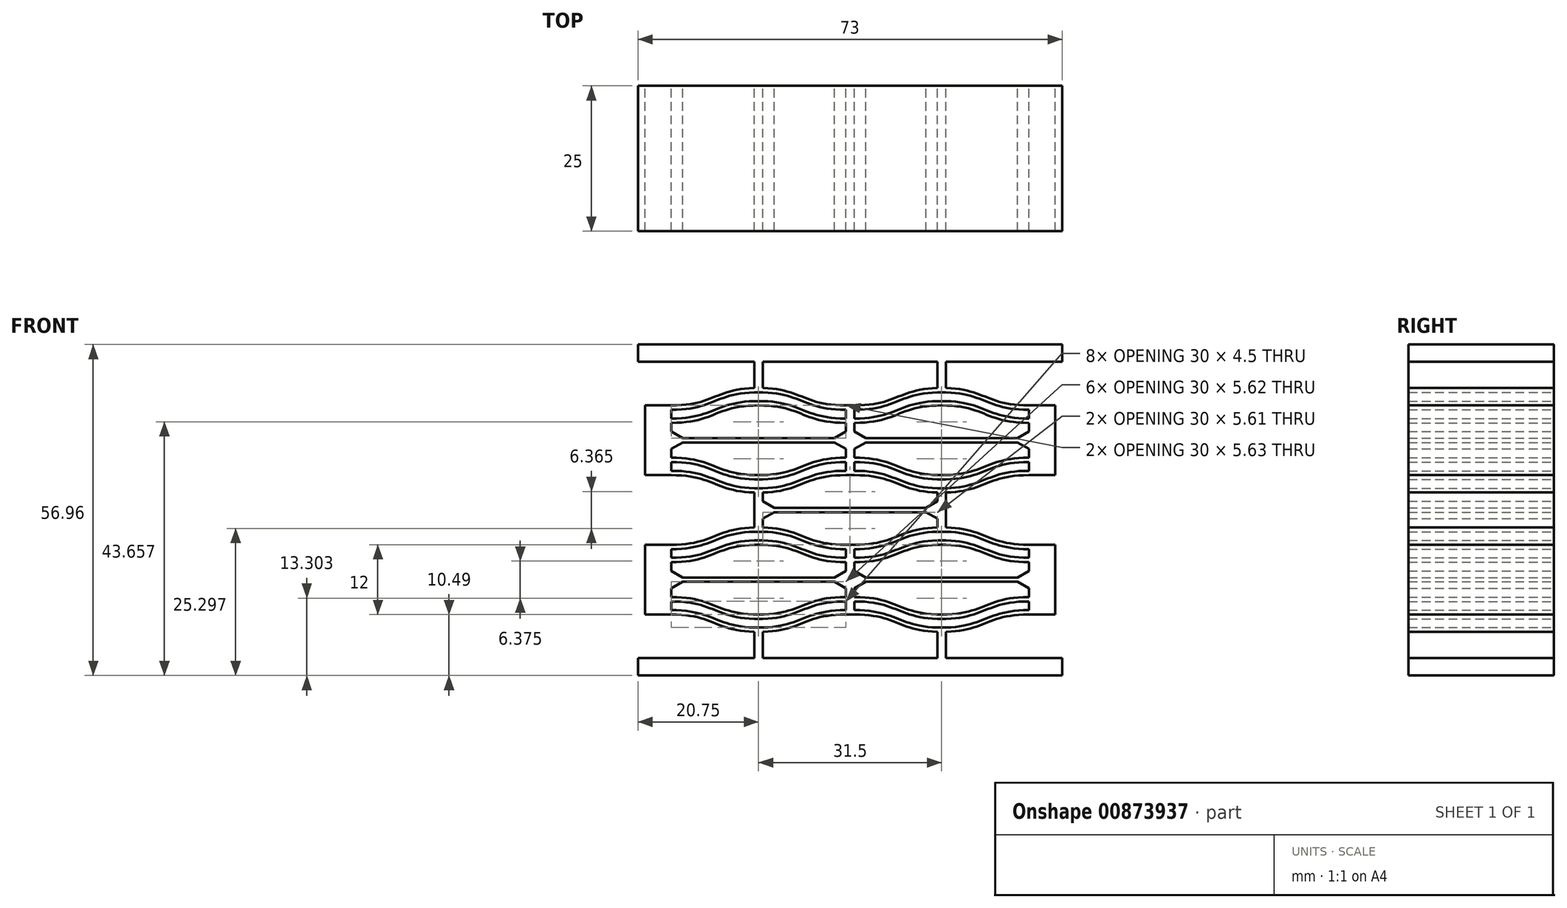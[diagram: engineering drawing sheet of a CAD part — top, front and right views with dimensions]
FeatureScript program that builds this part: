
annotation { "Feature Type Name" : "Feature", "Feature Type Description" : "" }
export const myFeature = defineFeature(function(context is Context, id is Id, definition is map)
    precondition{}
    {
        {
            var Q0;
            Q0=qCreatedBy(makeId("Front.planeOp"),FACE);
            var sketch = newSketch(context, id + "F0", { "sketchPlane" : qUnion([Q0])});
            skLineSegment(sketch, "E0", {"start": v(0, 11.25) * mm, "end": v(0, 9.75) * mm});
            skLineSegment(sketch, "E1", {"start": v(0, 0) * mm, "end": v(1.5, 0) * mm});
            skLineSegment(sketch, "E2", {"start": v(33, 12) * mm, "end": v(31.5, 12) * mm});
            skLineSegment(sketch, "E3", {"start": v(33, 0) * mm, "end": v(31.5, 0) * mm});
            skPoint(sketch, "E4", {"position": v(0, 6) * mm});
            skLineSegment(sketch, "E5", {"start": v(1.5, 11.25) * mm, "end": v(1.5, 9.75) * mm});
            skLineSegment(sketch, "E6", {"start": v(31.5, 11.25) * mm, "end": v(31.5, 9.75) * mm});
            skPoint(sketch, "E7", {"position": v(0, 7.5) * mm});
            skPoint(sketch, "E8", {"position": v(0, 4.5) * mm});
            skLineSegment(sketch, "E9", {"start": v(1.5, 4.5) * mm, "end": v(3.45, 5.62) * mm});
            skLineSegment(sketch, "E10", {"start": v(1.5, 7.5) * mm, "end": v(3.45, 6.38) * mm});
            skPoint(sketch, "E11", {"position": v(31.5, 4.5) * mm});
            skPoint(sketch, "E12", {"position": v(31.5, 7.5) * mm});
            skLineSegment(sketch, "E13", {"start": v(31.5, 7.5) * mm, "end": v(29.55, 6.38) * mm});
            skLineSegment(sketch, "E14", {"start": v(29.55, 5.63) * mm, "end": v(31.5, 4.5) * mm});
            skPoint(sketch, "E15.positionSnap0", {"position": v(16.5, 6.38) * mm});
            skPoint(sketch, "E16", {"position": v(0, 9) * mm});
            skPoint(sketch, "E17", {"position": v(0, 3) * mm});
            skPoint(sketch, "E18", {"position": v(0, 9.75) * mm});
            skPoint(sketch, "E19", {"position": v(0, 2.25) * mm});
            skPoint(sketch, "E20", {"position": v(1.5, 11.25) * mm});
            skPoint(sketch, "E21", {"position": v(1.5, 0.75) * mm});
            skPoint(sketch, "E22", {"position": v(1.5, 9.75) * mm});
            skPoint(sketch, "E23", {"position": v(1.5, 9) * mm});
            skPoint(sketch, "E24", {"position": v(1.5, 2.25) * mm});
            skPoint(sketch, "E25", {"position": v(1.5, 3) * mm});
            skPoint(sketch, "E26", {"position": v(31.5, 11.25) * mm});
            skPoint(sketch, "E27", {"position": v(31.5, 9.75) * mm});
            skPoint(sketch, "E28", {"position": v(31.5, 9) * mm});
            skPoint(sketch, "E29", {"position": v(31.5, 3) * mm});
            skPoint(sketch, "E30", {"position": v(31.5, 2.25) * mm});
            skPoint(sketch, "E31", {"position": v(31.5, 0.75) * mm});
            skLineSegment(sketch, "E32.trimOffspring", {"start": v(3.45, 6.38) * mm, "end": v(16.5, 6.38) * mm});
            skLineSegment(sketch, "E33.trimOffspring", {"start": v(3.45, 5.62) * mm, "end": v(29.55, 5.63) * mm});
            skPoint(sketch, "E34.start.orphan", {"position": v(0, 5.62) * mm});
            skLineSegment(sketch, "E35.trimOffspring", {"start": v(1.5, 9) * mm, "end": v(1.5, 7.5) * mm});
            skLineSegment(sketch, "E36.trimOffspring", {"start": v(1.5, 2.25) * mm, "end": v(1.5, 0.75) * mm});
            skLineSegment(sketch, "E37.trimOffspring", {"start": v(31.5, 9) * mm, "end": v(31.5, 7.5) * mm});
            skLineSegment(sketch, "E38.trimOffspring", {"start": v(31.5, 2.25) * mm, "end": v(31.5, 0.75) * mm});
            skLineSegment(sketch, "E39.trimOffspring", {"start": v(1.5, 4.5) * mm, "end": v(1.5, 3) * mm});
            skLineSegment(sketch, "E40.trimOffspring", {"start": v(31.5, 4.5) * mm, "end": v(31.5, 3) * mm});
            skLineSegment(sketch, "E41", {"start": v(16.5, 6.38) * mm, "end": v(29.55, 6.38) * mm});
            skPoint(sketch, "E42", {"position": v(16.5, 9) * mm});
            skPoint(sketch, "E43", {"position": v(16.5, 12) * mm});
            skPoint(sketch, "E44", {"position": v(9, 9) * mm});
            skPoint(sketch, "E45", {"position": v(9, 10.5) * mm});
            skPoint(sketch, "E46", {"position": v(24, 10.5) * mm});
            skFitSpline(sketch, "E47", {"points": [v(1.5, 9) * mm, v(9, 10.5) * mm, v(16.5, 12) * mm], "startDerivative": vector(22.5, 0) * mm, "endDerivative": vector(22.5, 0) * mm});
            skFitSpline(sketch, "E48", {"points": [v(16.5, 12) * mm, v(24, 10.5) * mm, v(31.5, 9) * mm], "startDerivative": vector(22.5, 0) * mm, "endDerivative": vector(22.5, 0) * mm});
            skFitSpline(sketch, "E49", {"points": [v(1.5, 9.75) * mm, v(9, 11.25) * mm, v(16.5, 12.75) * mm], "startDerivative": vector(22.5, 0) * mm, "endDerivative": vector(22.5, 0) * mm});
            skFitSpline(sketch, "E50", {"points": [v(16.5, 12.75) * mm, v(24, 11.25) * mm, v(31.5, 9.75) * mm], "startDerivative": vector(22.5, 0) * mm, "endDerivative": vector(22.5, 0) * mm});
            skFitSpline(sketch, "E51", {"points": [v(1.5, 11.25) * mm, v(9, 12.75) * mm, v(16.5, 14.25) * mm], "startDerivative": vector(22.5, 0) * mm, "endDerivative": vector(22.5, 0) * mm});
            skFitSpline(sketch, "E52", {"points": [v(16.5, 14.25) * mm, v(24, 12.75) * mm, v(31.5, 11.25) * mm], "startDerivative": vector(22.5, 0) * mm, "endDerivative": vector(22.5, 0) * mm});
            skFitSpline(sketch, "E53", {"points": [v(1.5, 12) * mm, v(9, 13.5) * mm, v(16.5, 15) * mm], "startDerivative": vector(22.5, 0) * mm, "endDerivative": vector(22.5, 0) * mm});
            skFitSpline(sketch, "E54", {"points": [v(16.5, 15) * mm, v(24, 13.5) * mm, v(31.5, 12) * mm], "startDerivative": vector(22.5, 0) * mm, "endDerivative": vector(22.5, 0) * mm});
            skFitSpline(sketch, "E55", {"points": [v(31.5, 3) * mm, v(24, 1.5) * mm, v(16.5, 0) * mm], "startDerivative": vector(-22.5, 0) * mm, "endDerivative": vector(-22.5, 0) * mm});
            skFitSpline(sketch, "E56", {"points": [v(16.5, 0) * mm, v(9, 1.5) * mm, v(1.5, 3) * mm], "startDerivative": vector(-22.5, 0) * mm, "endDerivative": vector(-22.5, 0) * mm});
            skFitSpline(sketch, "E57", {"points": [v(31.5, 2.25) * mm, v(24, 0.75) * mm, v(16.5, -0.75) * mm], "startDerivative": vector(-22.5, 0) * mm, "endDerivative": vector(-22.5, 0) * mm});
            skFitSpline(sketch, "E58", {"points": [v(16.5, -0.75) * mm, v(9, 0.75) * mm, v(1.5, 2.25) * mm], "startDerivative": vector(-22.5, 0) * mm, "endDerivative": vector(-22.5, 0) * mm});
            skFitSpline(sketch, "E59", {"points": [v(31.5, 0.75) * mm, v(24, -0.75) * mm, v(16.5, -2.25) * mm], "startDerivative": vector(-22.5, 0) * mm, "endDerivative": vector(-22.5, 0) * mm});
            skFitSpline(sketch, "E60", {"points": [v(16.5, -2.25) * mm, v(9, -0.75) * mm, v(1.5, 0.75) * mm], "startDerivative": vector(-22.5, 0) * mm, "endDerivative": vector(-22.5, 0) * mm});
            skFitSpline(sketch, "E61", {"points": [v(31.5, 0) * mm, v(24, -1.5) * mm, v(16.5, -3) * mm], "startDerivative": vector(-22.5, 0) * mm, "endDerivative": vector(-22.5, 0) * mm});
            skFitSpline(sketch, "E62", {"points": [v(16.5, -3) * mm, v(9, -1.5) * mm, v(1.5, 0) * mm], "startDerivative": vector(-22.5, 0) * mm, "endDerivative": vector(-22.5, 0) * mm});
            skPoint(sketch, "E63", {"position": v(15.75, -0.34) * mm});
            skPoint(sketch, "E64", {"position": v(17.25, -0.34) * mm});
            skLineSegment(sketch, "E65", {"start": v(15.75, -0.74) * mm, "end": v(15.75, -2.24) * mm});
            skLineSegment(sketch, "E66", {"start": v(17.25, -0.74) * mm, "end": v(17.25, -2.24) * mm});
            skLineSegment(sketch, "E67", {"start": v(15.75, -2.99) * mm, "end": v(15.75, -7.49) * mm});
            skLineSegment(sketch, "E68", {"start": v(15.75, 12.74) * mm, "end": v(15.75, 14.24) * mm});
            skLineSegment(sketch, "E69", {"start": v(17.25, 14.24) * mm, "end": v(17.25, 12.74) * mm});
            skLineSegment(sketch, "E70", {"start": v(17.25, -7.49) * mm, "end": v(17.25, -2.99) * mm});
            skPoint(sketch, "E71", {"position": v(15.75, 14.99) * mm});
            skPoint(sketch, "E72", {"position": v(17.25, 14.99) * mm});
            skLineSegment(sketch, "E73", {"start": v(15.75, 14.99) * mm, "end": v(15.75, 16.49) * mm});
            skLineSegment(sketch, "E74", {"start": v(15.75, 19.49) * mm, "end": v(17.25, 19.49) * mm});
            skLineSegment(sketch, "E75", {"start": v(17.25, 19.49) * mm, "end": v(17.25, 14.99) * mm});
            skLineSegment(sketch, "E76", {"start": v(-31.5, 0) * mm, "end": v(-30, 0) * mm});
            skLineSegment(sketch, "E77", {"start": v(-31.5, 12) * mm, "end": v(-30, 12) * mm});
            skLineSegment(sketch, "E78", {"start": v(1.5, 12) * mm, "end": v(0, 12) * mm});
            skLineSegment(sketch, "E79", {"start": v(1.5, 0) * mm, "end": v(0, 0) * mm});
            skLineSegment(sketch, "E80", {"start": v(-30, 11.25) * mm, "end": v(-30, 9.75) * mm});
            skLineSegment(sketch, "E81", {"start": v(-30, 4.5) * mm, "end": v(-28.05, 5.62) * mm});
            skLineSegment(sketch, "E82", {"start": v(-30, 7.5) * mm, "end": v(-28.05, 6.38) * mm});
            skLineSegment(sketch, "E83", {"start": v(0, 7.5) * mm, "end": v(-1.95, 6.38) * mm});
            skLineSegment(sketch, "E84", {"start": v(-1.95, 5.63) * mm, "end": v(0, 4.5) * mm});
            skPoint(sketch, "E85.positionSnap0", {"position": v(-15, 6.37) * mm});
            skPoint(sketch, "E86", {"position": v(-30, 11.25) * mm});
            skPoint(sketch, "E87", {"position": v(-30, 0.75) * mm});
            skPoint(sketch, "E88", {"position": v(-30, 9.75) * mm});
            skPoint(sketch, "E89", {"position": v(-30, 9) * mm});
            skPoint(sketch, "E90", {"position": v(-30, 2.25) * mm});
            skPoint(sketch, "E91", {"position": v(-30, 3) * mm});
            skPoint(sketch, "E92", {"position": v(0, 11.25) * mm});
            skPoint(sketch, "E93", {"position": v(0, 0.75) * mm});
            skLineSegment(sketch, "E94.trimOffspring", {"start": v(-28.05, 6.38) * mm, "end": v(-15, 6.38) * mm});
            skLineSegment(sketch, "E95.trimOffspring", {"start": v(-28.05, 5.62) * mm, "end": v(-1.95, 5.63) * mm});
            skLineSegment(sketch, "E96.trimOffspring", {"start": v(-30, 9) * mm, "end": v(-30, 7.5) * mm});
            skLineSegment(sketch, "E97.trimOffspring", {"start": v(-30, 2.25) * mm, "end": v(-30, 0.75) * mm});
            skPoint(sketch, "E98.trimOffspring.end.orphan", {"position": v(1.5, 5.63) * mm});
            skLineSegment(sketch, "E99.trimOffspring", {"start": v(0, 9) * mm, "end": v(0, 7.5) * mm});
            skLineSegment(sketch, "E100.trimOffspring", {"start": v(0, 2.25) * mm, "end": v(0, 0.75) * mm});
            skLineSegment(sketch, "E101.trimOffspring", {"start": v(-30, 4.5) * mm, "end": v(-30, 3) * mm});
            skLineSegment(sketch, "E102.trimOffspring", {"start": v(0, 4.5) * mm, "end": v(0, 3) * mm});
            skLineSegment(sketch, "E103", {"start": v(-15, 6.38) * mm, "end": v(-1.95, 6.38) * mm});
            skPoint(sketch, "E104", {"position": v(-15, 9) * mm});
            skPoint(sketch, "E105", {"position": v(-15, 12) * mm});
            skPoint(sketch, "E106", {"position": v(-22.5, 9) * mm});
            skPoint(sketch, "E107", {"position": v(-22.5, 10.5) * mm});
            skPoint(sketch, "E108", {"position": v(-7.5, 10.5) * mm});
            skFitSpline(sketch, "E109", {"points": [v(-30, 9) * mm, v(-22.5, 10.5) * mm, v(-15, 12) * mm], "startDerivative": vector(22.5, 0) * mm, "endDerivative": vector(22.5, 0) * mm});
            skFitSpline(sketch, "E110", {"points": [v(-15, 12) * mm, v(-7.5, 10.5) * mm, v(0, 9) * mm], "startDerivative": vector(22.5, 0) * mm, "endDerivative": vector(22.5, 0) * mm});
            skFitSpline(sketch, "E111", {"points": [v(-30, 9.75) * mm, v(-22.5, 11.25) * mm, v(-15, 12.75) * mm], "startDerivative": vector(22.5, 0) * mm, "endDerivative": vector(22.5, 0) * mm});
            skFitSpline(sketch, "E112", {"points": [v(-15, 12.75) * mm, v(-7.5, 11.25) * mm, v(0, 9.75) * mm], "startDerivative": vector(22.5, 0) * mm, "endDerivative": vector(22.5, 0) * mm});
            skFitSpline(sketch, "E113", {"points": [v(-30, 11.25) * mm, v(-22.5, 12.75) * mm, v(-15, 14.25) * mm], "startDerivative": vector(22.5, 0) * mm, "endDerivative": vector(22.5, 0) * mm});
            skFitSpline(sketch, "E114", {"points": [v(-15, 14.25) * mm, v(-7.5, 12.75) * mm, v(0, 11.25) * mm], "startDerivative": vector(22.5, 0) * mm, "endDerivative": vector(22.5, 0) * mm});
            skFitSpline(sketch, "E115", {"points": [v(-30, 12) * mm, v(-22.5, 13.5) * mm, v(-15, 15) * mm], "startDerivative": vector(22.5, 0) * mm, "endDerivative": vector(22.5, 0) * mm});
            skFitSpline(sketch, "E116", {"points": [v(-15, 15) * mm, v(-7.5, 13.5) * mm, v(0, 12) * mm], "startDerivative": vector(22.5, 0) * mm, "endDerivative": vector(22.5, 0) * mm});
            skFitSpline(sketch, "E117", {"points": [v(0, 3) * mm, v(-7.5, 1.5) * mm, v(-15, 0) * mm], "startDerivative": vector(-22.5, 0) * mm, "endDerivative": vector(-22.5, 0) * mm});
            skFitSpline(sketch, "E118", {"points": [v(-15, 0) * mm, v(-22.5, 1.5) * mm, v(-30, 3) * mm], "startDerivative": vector(-22.5, 0) * mm, "endDerivative": vector(-22.5, 0) * mm});
            skFitSpline(sketch, "E119", {"points": [v(0, 2.25) * mm, v(-7.5, 0.75) * mm, v(-15, -0.75) * mm], "startDerivative": vector(-22.5, 0) * mm, "endDerivative": vector(-22.5, 0) * mm});
            skFitSpline(sketch, "E120", {"points": [v(-15, -0.75) * mm, v(-22.5, 0.75) * mm, v(-30, 2.25) * mm], "startDerivative": vector(-22.5, 0) * mm, "endDerivative": vector(-22.5, 0) * mm});
            skFitSpline(sketch, "E121", {"points": [v(0, 0.75) * mm, v(-7.5, -0.75) * mm, v(-15, -2.25) * mm], "startDerivative": vector(-22.5, 0) * mm, "endDerivative": vector(-22.5, 0) * mm});
            skFitSpline(sketch, "E122", {"points": [v(-15, -2.25) * mm, v(-22.5, -0.75) * mm, v(-30, 0.75) * mm], "startDerivative": vector(-22.5, 0) * mm, "endDerivative": vector(-22.5, 0) * mm});
            skFitSpline(sketch, "E123", {"points": [v(0, 0) * mm, v(-7.5, -1.5) * mm, v(-15, -3) * mm], "startDerivative": vector(-22.5, 0) * mm, "endDerivative": vector(-22.5, 0) * mm});
            skFitSpline(sketch, "E124", {"points": [v(-15, -3) * mm, v(-22.5, -1.5) * mm, v(-30, 0) * mm], "startDerivative": vector(-22.5, 0) * mm, "endDerivative": vector(-22.5, 0) * mm});
            skPoint(sketch, "E125", {"position": v(-15.75, -0.34) * mm});
            skPoint(sketch, "E126", {"position": v(-14.25, -0.34) * mm});
            skLineSegment(sketch, "E127", {"start": v(-15.75, -0.74) * mm, "end": v(-15.75, -2.24) * mm});
            skLineSegment(sketch, "E128", {"start": v(-14.25, -0.74) * mm, "end": v(-14.25, -2.24) * mm});
            skLineSegment(sketch, "E129", {"start": v(-15.75, -2.99) * mm, "end": v(-15.75, -7.49) * mm});
            skLineSegment(sketch, "E130", {"start": v(-15.75, 12.74) * mm, "end": v(-15.75, 14.24) * mm});
            skLineSegment(sketch, "E131", {"start": v(-14.25, 14.24) * mm, "end": v(-14.25, 12.74) * mm});
            skLineSegment(sketch, "E132", {"start": v(-14.25, -7.49) * mm, "end": v(-14.25, -2.99) * mm});
            skPoint(sketch, "E133", {"position": v(-15.75, 14.99) * mm});
            skPoint(sketch, "E134", {"position": v(-14.25, 14.99) * mm});
            skLineSegment(sketch, "E135", {"start": v(-15.75, 14.99) * mm, "end": v(-15.75, 19.49) * mm});
            skLineSegment(sketch, "E136", {"start": v(-14.25, 16.49) * mm, "end": v(-14.25, 14.99) * mm});
            skLineSegment(sketch, "E137", {"start": v(-15.75, 23.99) * mm, "end": v(-15.75, 14.99) * mm});
            skLineSegment(sketch, "E138", {"start": v(17.25, 23.99) * mm, "end": v(17.25, 14.99) * mm});
            skLineSegment(sketch, "E139", {"start": v(-15.75, 11.99) * mm, "end": v(-14.25, 11.99) * mm});
            skLineSegment(sketch, "E140", {"start": v(-15.75, 23.99) * mm, "end": v(-14.25, 23.99) * mm});
            skLineSegment(sketch, "E141", {"start": v(17.25, 23.99) * mm, "end": v(15.75, 23.99) * mm});
            skLineSegment(sketch, "E142", {"start": v(17.25, 11.99) * mm, "end": v(15.75, 11.99) * mm});
            skPoint(sketch, "E143", {"position": v(-15.75, 17.99) * mm});
            skLineSegment(sketch, "E144", {"start": v(-14.25, 23.24) * mm, "end": v(-14.25, 21.74) * mm});
            skLineSegment(sketch, "E145", {"start": v(15.75, 23.24) * mm, "end": v(15.75, 21.74) * mm});
            skPoint(sketch, "E146", {"position": v(-15.75, 19.49) * mm});
            skPoint(sketch, "E147", {"position": v(-15.75, 16.49) * mm});
            skLineSegment(sketch, "E148", {"start": v(-14.25, 16.49) * mm, "end": v(-12.3, 17.61) * mm});
            skLineSegment(sketch, "E149", {"start": v(-14.25, 19.49) * mm, "end": v(-12.3, 18.36) * mm});
            skPoint(sketch, "E150", {"position": v(15.75, 16.49) * mm});
            skPoint(sketch, "E151", {"position": v(15.75, 19.49) * mm});
            skLineSegment(sketch, "E152", {"start": v(15.75, 19.49) * mm, "end": v(13.8, 18.36) * mm});
            skLineSegment(sketch, "E153", {"start": v(13.8, 17.61) * mm, "end": v(15.75, 16.49) * mm});
            skPoint(sketch, "E154.positionSnap0", {"position": v(0.75, 18.36) * mm});
            skPoint(sketch, "E155", {"position": v(-15.75, 20.99) * mm});
            skPoint(sketch, "E156", {"position": v(-15.75, 21.74) * mm});
            skPoint(sketch, "E157", {"position": v(-15.75, 14.24) * mm});
            skPoint(sketch, "E158", {"position": v(-14.25, 23.24) * mm});
            skPoint(sketch, "E159", {"position": v(-14.25, 12.74) * mm});
            skPoint(sketch, "E160", {"position": v(-14.25, 21.74) * mm});
            skPoint(sketch, "E161", {"position": v(-14.25, 20.99) * mm});
            skPoint(sketch, "E162", {"position": v(-14.25, 14.24) * mm});
            skPoint(sketch, "E163", {"position": v(15.75, 23.24) * mm});
            skPoint(sketch, "E164", {"position": v(15.75, 21.74) * mm});
            skPoint(sketch, "E165", {"position": v(15.75, 20.99) * mm});
            skPoint(sketch, "E166", {"position": v(15.75, 14.24) * mm});
            skPoint(sketch, "E167", {"position": v(15.75, 12.74) * mm});
            skLineSegment(sketch, "E168.trimOffspring", {"start": v(-12.3, 18.36) * mm, "end": v(0.75, 18.36) * mm});
            skLineSegment(sketch, "E169.trimOffspring", {"start": v(-12.3, 17.61) * mm, "end": v(13.8, 17.61) * mm});
            skPoint(sketch, "E170.start.orphan", {"position": v(-15.75, 17.61) * mm});
            skPoint(sketch, "E171.start.orphan", {"position": v(-15.75, 18.36) * mm});
            skLineSegment(sketch, "E172.trimOffspring", {"start": v(-14.25, 20.99) * mm, "end": v(-14.25, 19.49) * mm});
            skPoint(sketch, "E173.trimOffspring.end.orphan", {"position": v(17.25, 17.61) * mm});
            skPoint(sketch, "E174.trimOffspring.end.orphan", {"position": v(17.25, 18.36) * mm});
            skLineSegment(sketch, "E175.trimOffspring", {"start": v(15.75, 20.99) * mm, "end": v(15.75, 19.49) * mm});
            skLineSegment(sketch, "E176.trimOffspring", {"start": v(15.75, 14.24) * mm, "end": v(15.75, 12.74) * mm});
            skLineSegment(sketch, "E177.trimOffspring", {"start": v(15.75, 16.49) * mm, "end": v(15.75, 14.99) * mm});
            skLineSegment(sketch, "E178", {"start": v(0.75, 18.36) * mm, "end": v(13.8, 18.36) * mm});
            skPoint(sketch, "E179", {"position": v(0.75, 20.99) * mm});
            skPoint(sketch, "E180", {"position": v(0.75, 23.99) * mm});
            skPoint(sketch, "E181", {"position": v(-6.75, 20.99) * mm});
            skPoint(sketch, "E182", {"position": v(-6.75, 22.49) * mm});
            skPoint(sketch, "E183", {"position": v(8.25, 22.49) * mm});
            skPoint(sketch, "E184", {"position": v(0, 11.65) * mm});
            skPoint(sketch, "E185", {"position": v(1.5, 11.65) * mm});
            skLineSegment(sketch, "E186", {"start": v(0, 24.73) * mm, "end": v(0, 26.23) * mm});
            skLineSegment(sketch, "E187", {"start": v(1.5, 26.23) * mm, "end": v(1.5, 24.73) * mm});
            skPoint(sketch, "E188", {"position": v(0, 26.98) * mm});
            skPoint(sketch, "E189", {"position": v(1.5, 26.98) * mm});
            skLineSegment(sketch, "E190", {"start": v(0, 26.98) * mm, "end": v(0, 28.48) * mm});
            skLineSegment(sketch, "E191.trimOffspring", {"start": v(0, 6) * mm, "end": v(0, 5.62) * mm});
            skPoint(sketch, "E192.orphan", {"position": v(-14.25, 19.49) * mm});
            skLineSegment(sketch, "E193.trimOffspring", {"start": v(1.5, 7.5) * mm, "end": v(1.5, 9) * mm});
            skPoint(sketch, "E194.start.orphan", {"position": v(1.5, 4.5) * mm});
            skLineSegment(sketch, "E195.trimOffspring", {"start": v(-15.75, 14.24) * mm, "end": v(-15.75, 12.74) * mm});
            skLineSegment(sketch, "E196", {"start": v(1.5, 35.23) * mm, "end": v(1.5, 33.73) * mm});
            skLineSegment(sketch, "E197", {"start": v(-31.5, 23.98) * mm, "end": v(-30, 23.98) * mm});
            skLineSegment(sketch, "E198", {"start": v(-31.5, 35.98) * mm, "end": v(-30, 35.98) * mm});
            skLineSegment(sketch, "E199", {"start": v(1.5, 35.98) * mm, "end": v(0, 35.98) * mm});
            skLineSegment(sketch, "E200", {"start": v(1.5, 23.98) * mm, "end": v(0, 23.98) * mm});
            skLineSegment(sketch, "E201", {"start": v(-30, 35.23) * mm, "end": v(-30, 33.73) * mm});
            skLineSegment(sketch, "E202", {"start": v(0, 35.23) * mm, "end": v(0, 33.73) * mm});
            skLineSegment(sketch, "E203", {"start": v(-30, 28.48) * mm, "end": v(-28.05, 29.6) * mm});
            skLineSegment(sketch, "E204", {"start": v(-30, 31.48) * mm, "end": v(-28.05, 30.35) * mm});
            skPoint(sketch, "E205", {"position": v(0, 28.48) * mm});
            skPoint(sketch, "E206", {"position": v(0, 31.48) * mm});
            skLineSegment(sketch, "E207", {"start": v(0, 31.48) * mm, "end": v(-1.95, 30.35) * mm});
            skLineSegment(sketch, "E208", {"start": v(-1.95, 29.6) * mm, "end": v(0, 28.48) * mm});
            skPoint(sketch, "E209.positionSnap0", {"position": v(-15, 30.35) * mm});
            skPoint(sketch, "E210", {"position": v(-30, 35.23) * mm});
            skPoint(sketch, "E211", {"position": v(-30, 24.73) * mm});
            skPoint(sketch, "E212", {"position": v(-30, 33.73) * mm});
            skPoint(sketch, "E213", {"position": v(-30, 32.98) * mm});
            skPoint(sketch, "E214", {"position": v(-30, 26.23) * mm});
            skPoint(sketch, "E215", {"position": v(-30, 26.98) * mm});
            skPoint(sketch, "E216", {"position": v(0, 35.23) * mm});
            skPoint(sketch, "E217", {"position": v(0, 33.73) * mm});
            skPoint(sketch, "E218", {"position": v(0, 32.98) * mm});
            skPoint(sketch, "E219", {"position": v(0, 26.23) * mm});
            skPoint(sketch, "E220", {"position": v(0, 24.73) * mm});
            skLineSegment(sketch, "E221.trimOffspring", {"start": v(-28.05, 30.35) * mm, "end": v(-15, 30.35) * mm});
            skLineSegment(sketch, "E222.trimOffspring", {"start": v(-28.05, 29.6) * mm, "end": v(-1.95, 29.6) * mm});
            skLineSegment(sketch, "E223.trimOffspring", {"start": v(-30, 32.98) * mm, "end": v(-30, 31.48) * mm});
            skLineSegment(sketch, "E224.trimOffspring", {"start": v(-30, 26.23) * mm, "end": v(-30, 24.73) * mm});
            skPoint(sketch, "E225.trimOffspring.end.orphan", {"position": v(1.5, 29.6) * mm});
            skPoint(sketch, "E226.trimOffspring.end.orphan", {"position": v(1.5, 30.35) * mm});
            skLineSegment(sketch, "E227.trimOffspring", {"start": v(0, 32.98) * mm, "end": v(0, 31.48) * mm});
            skLineSegment(sketch, "E228.trimOffspring", {"start": v(0, 26.23) * mm, "end": v(0, 24.73) * mm});
            skLineSegment(sketch, "E229.trimOffspring", {"start": v(-30, 28.48) * mm, "end": v(-30, 26.98) * mm});
            skLineSegment(sketch, "E230.trimOffspring", {"start": v(0, 28.48) * mm, "end": v(0, 26.98) * mm});
            skLineSegment(sketch, "E231", {"start": v(-15, 30.35) * mm, "end": v(-1.95, 30.35) * mm});
            skPoint(sketch, "E232", {"position": v(-15, 32.98) * mm});
            skPoint(sketch, "E233", {"position": v(-15, 35.98) * mm});
            skPoint(sketch, "E234", {"position": v(-22.5, 32.98) * mm});
            skPoint(sketch, "E235", {"position": v(-22.5, 34.48) * mm});
            skPoint(sketch, "E236", {"position": v(-7.5, 34.48) * mm});
            skFitSpline(sketch, "E237", {"points": [v(-30, 32.98) * mm, v(-22.5, 34.48) * mm, v(-15, 35.98) * mm], "startDerivative": vector(22.5, 0) * mm, "endDerivative": vector(22.5, 0) * mm});
            skFitSpline(sketch, "E238", {"points": [v(-15, 35.98) * mm, v(-7.5, 34.48) * mm, v(0, 32.98) * mm], "startDerivative": vector(22.5, 0) * mm, "endDerivative": vector(22.5, 0) * mm});
            skFitSpline(sketch, "E239", {"points": [v(-30, 33.73) * mm, v(-22.5, 35.23) * mm, v(-15, 36.73) * mm], "startDerivative": vector(22.5, 0) * mm, "endDerivative": vector(22.5, 0) * mm});
            skFitSpline(sketch, "E240", {"points": [v(-15, 36.73) * mm, v(-7.5, 35.23) * mm, v(0, 33.73) * mm], "startDerivative": vector(22.5, 0) * mm, "endDerivative": vector(22.5, 0) * mm});
            skFitSpline(sketch, "E241", {"points": [v(-30, 35.23) * mm, v(-22.5, 36.73) * mm, v(-15, 38.23) * mm], "startDerivative": vector(22.5, 0) * mm, "endDerivative": vector(22.5, 0) * mm});
            skFitSpline(sketch, "E242", {"points": [v(-15, 38.23) * mm, v(-7.5, 36.73) * mm, v(0, 35.23) * mm], "startDerivative": vector(22.5, 0) * mm, "endDerivative": vector(22.5, 0) * mm});
            skFitSpline(sketch, "E243", {"points": [v(-30, 35.98) * mm, v(-22.5, 37.48) * mm, v(-15, 38.98) * mm], "startDerivative": vector(22.5, 0) * mm, "endDerivative": vector(22.5, 0) * mm});
            skFitSpline(sketch, "E244", {"points": [v(-15, 38.98) * mm, v(-7.5, 37.48) * mm, v(0, 35.98) * mm], "startDerivative": vector(22.5, 0) * mm, "endDerivative": vector(22.5, 0) * mm});
            skFitSpline(sketch, "E245", {"points": [v(0, 26.98) * mm, v(-7.5, 25.48) * mm, v(-15, 23.98) * mm], "startDerivative": vector(-22.5, 0) * mm, "endDerivative": vector(-22.5, 0) * mm});
            skFitSpline(sketch, "E246", {"points": [v(-15, 23.98) * mm, v(-22.5, 25.48) * mm, v(-30, 26.98) * mm], "startDerivative": vector(-22.5, 0) * mm, "endDerivative": vector(-22.5, 0) * mm});
            skFitSpline(sketch, "E247", {"points": [v(0, 26.23) * mm, v(-7.5, 24.73) * mm, v(-15, 23.23) * mm], "startDerivative": vector(-22.5, 0) * mm, "endDerivative": vector(-22.5, 0) * mm});
            skFitSpline(sketch, "E248", {"points": [v(-15, 23.23) * mm, v(-22.5, 24.73) * mm, v(-30, 26.23) * mm], "startDerivative": vector(-22.5, 0) * mm, "endDerivative": vector(-22.5, 0) * mm});
            skFitSpline(sketch, "E249", {"points": [v(0, 24.73) * mm, v(-7.5, 23.23) * mm, v(-15, 21.73) * mm], "startDerivative": vector(-22.5, 0) * mm, "endDerivative": vector(-22.5, 0) * mm});
            skFitSpline(sketch, "E250", {"points": [v(-15, 21.73) * mm, v(-22.5, 23.23) * mm, v(-30, 24.73) * mm], "startDerivative": vector(-22.5, 0) * mm, "endDerivative": vector(-22.5, 0) * mm});
            skFitSpline(sketch, "E251", {"points": [v(0, 23.98) * mm, v(-7.5, 22.48) * mm, v(-15, 20.98) * mm], "startDerivative": vector(-22.5, 0) * mm, "endDerivative": vector(-22.5, 0) * mm});
            skFitSpline(sketch, "E252", {"points": [v(-15, 20.98) * mm, v(-22.5, 22.48) * mm, v(-30, 23.98) * mm], "startDerivative": vector(-22.5, 0) * mm, "endDerivative": vector(-22.5, 0) * mm});
            skPoint(sketch, "E253", {"position": v(-15.75, 23.64) * mm});
            skPoint(sketch, "E254", {"position": v(-14.25, 23.64) * mm});
            skLineSegment(sketch, "E255", {"start": v(-15.75, 23.24) * mm, "end": v(-15.75, 21.74) * mm});
            skLineSegment(sketch, "E256", {"start": v(-15.75, 20.99) * mm, "end": v(-15.75, 16.49) * mm});
            skLineSegment(sketch, "E257", {"start": v(-15.75, 36.72) * mm, "end": v(-15.75, 38.22) * mm});
            skLineSegment(sketch, "E258", {"start": v(-14.25, 38.22) * mm, "end": v(-14.25, 36.72) * mm});
            skLineSegment(sketch, "E259", {"start": v(-14.25, 19.49) * mm, "end": v(-14.25, 20.99) * mm});
            skPoint(sketch, "E260", {"position": v(-15.75, 38.97) * mm});
            skPoint(sketch, "E261", {"position": v(-14.25, 38.97) * mm});
            skLineSegment(sketch, "E262", {"start": v(-15.75, 38.97) * mm, "end": v(-15.75, 43.47) * mm});
            skLineSegment(sketch, "E263", {"start": v(-14.25, 43.47) * mm, "end": v(-14.25, 38.97) * mm});
            skPoint(sketch, "E264.end.orphan", {"position": v(-14.25, 16.49) * mm});
            skLineSegment(sketch, "E265", {"start": v(0, 23.98) * mm, "end": v(1.5, 23.98) * mm});
            skLineSegment(sketch, "E266", {"start": v(0, 35.98) * mm, "end": v(1.5, 35.98) * mm});
            skLineSegment(sketch, "E267", {"start": v(33, 35.98) * mm, "end": v(31.5, 35.98) * mm});
            skLineSegment(sketch, "E268", {"start": v(33, 23.98) * mm, "end": v(31.5, 23.98) * mm});
            skPoint(sketch, "E269", {"position": v(0, 29.98) * mm});
            skLineSegment(sketch, "E270", {"start": v(31.5, 35.23) * mm, "end": v(31.5, 33.73) * mm});
            skLineSegment(sketch, "E271", {"start": v(1.5, 28.48) * mm, "end": v(3.45, 29.6) * mm});
            skLineSegment(sketch, "E272", {"start": v(1.5, 31.48) * mm, "end": v(3.45, 30.35) * mm});
            skPoint(sketch, "E273", {"position": v(31.5, 28.48) * mm});
            skPoint(sketch, "E274", {"position": v(31.5, 31.48) * mm});
            skLineSegment(sketch, "E275", {"start": v(31.5, 31.48) * mm, "end": v(29.55, 30.35) * mm});
            skLineSegment(sketch, "E276", {"start": v(29.55, 29.6) * mm, "end": v(31.5, 28.48) * mm});
            skPoint(sketch, "E277.positionSnap0", {"position": v(16.5, 30.35) * mm});
            skPoint(sketch, "E278", {"position": v(1.5, 35.23) * mm});
            skPoint(sketch, "E279", {"position": v(1.5, 24.73) * mm});
            skPoint(sketch, "E280", {"position": v(1.5, 33.73) * mm});
            skPoint(sketch, "E281", {"position": v(1.5, 32.98) * mm});
            skPoint(sketch, "E282", {"position": v(1.5, 26.23) * mm});
            skPoint(sketch, "E283", {"position": v(31.5, 35.23) * mm});
            skPoint(sketch, "E284", {"position": v(31.5, 33.73) * mm});
            skPoint(sketch, "E285", {"position": v(31.5, 32.98) * mm});
            skPoint(sketch, "E286", {"position": v(31.5, 26.98) * mm});
            skPoint(sketch, "E287", {"position": v(31.5, 26.23) * mm});
            skPoint(sketch, "E288", {"position": v(31.5, 24.73) * mm});
            skLineSegment(sketch, "E289.trimOffspring", {"start": v(3.45, 30.35) * mm, "end": v(16.5, 30.35) * mm});
            skLineSegment(sketch, "E290.trimOffspring", {"start": v(3.45, 29.6) * mm, "end": v(29.55, 29.6) * mm});
            skPoint(sketch, "E291.start.orphan", {"position": v(0, 29.6) * mm});
            skPoint(sketch, "E292.start.orphan", {"position": v(0, 30.35) * mm});
            skLineSegment(sketch, "E293.trimOffspring", {"start": v(1.5, 32.98) * mm, "end": v(1.5, 31.48) * mm});
            skLineSegment(sketch, "E294.trimOffspring", {"start": v(31.5, 32.98) * mm, "end": v(31.5, 31.48) * mm});
            skLineSegment(sketch, "E295.trimOffspring", {"start": v(31.5, 26.23) * mm, "end": v(31.5, 24.73) * mm});
            skLineSegment(sketch, "E296.trimOffspring", {"start": v(1.5, 28.48) * mm, "end": v(1.5, 26.98) * mm});
            skLineSegment(sketch, "E297.trimOffspring", {"start": v(31.5, 28.48) * mm, "end": v(31.5, 26.98) * mm});
            skLineSegment(sketch, "E298", {"start": v(16.5, 30.35) * mm, "end": v(29.55, 30.35) * mm});
            skPoint(sketch, "E299", {"position": v(16.5, 32.98) * mm});
            skPoint(sketch, "E300", {"position": v(16.5, 35.98) * mm});
            skPoint(sketch, "E301", {"position": v(9, 32.98) * mm});
            skPoint(sketch, "E302", {"position": v(9, 34.48) * mm});
            skPoint(sketch, "E303", {"position": v(24, 34.48) * mm});
            skFitSpline(sketch, "E304", {"points": [v(1.5, 32.98) * mm, v(9, 34.48) * mm, v(16.5, 35.98) * mm], "startDerivative": vector(22.5, 0) * mm, "endDerivative": vector(22.5, 0) * mm});
            skFitSpline(sketch, "E305", {"points": [v(16.5, 35.98) * mm, v(24, 34.48) * mm, v(31.5, 32.98) * mm], "startDerivative": vector(22.5, 0) * mm, "endDerivative": vector(22.5, 0) * mm});
            skFitSpline(sketch, "E306", {"points": [v(1.5, 33.73) * mm, v(9, 35.23) * mm, v(16.5, 36.73) * mm], "startDerivative": vector(22.5, 0) * mm, "endDerivative": vector(22.5, 0) * mm});
            skFitSpline(sketch, "E307", {"points": [v(16.5, 36.73) * mm, v(24, 35.23) * mm, v(31.5, 33.73) * mm], "startDerivative": vector(22.5, 0) * mm, "endDerivative": vector(22.5, 0) * mm});
            skFitSpline(sketch, "E308", {"points": [v(1.5, 35.23) * mm, v(9, 36.73) * mm, v(16.5, 38.23) * mm], "startDerivative": vector(22.5, 0) * mm, "endDerivative": vector(22.5, 0) * mm});
            skFitSpline(sketch, "E309", {"points": [v(16.5, 38.23) * mm, v(24, 36.73) * mm, v(31.5, 35.23) * mm], "startDerivative": vector(22.5, 0) * mm, "endDerivative": vector(22.5, 0) * mm});
            skFitSpline(sketch, "E310", {"points": [v(1.5, 35.98) * mm, v(9, 37.48) * mm, v(16.5, 38.98) * mm], "startDerivative": vector(22.5, 0) * mm, "endDerivative": vector(22.5, 0) * mm});
            skFitSpline(sketch, "E311", {"points": [v(16.5, 38.98) * mm, v(24, 37.48) * mm, v(31.5, 35.98) * mm], "startDerivative": vector(22.5, 0) * mm, "endDerivative": vector(22.5, 0) * mm});
            skFitSpline(sketch, "E312", {"points": [v(31.5, 26.98) * mm, v(24, 25.48) * mm, v(16.5, 23.98) * mm], "startDerivative": vector(-22.5, 0) * mm, "endDerivative": vector(-22.5, 0) * mm});
            skFitSpline(sketch, "E313", {"points": [v(16.5, 23.98) * mm, v(9, 25.48) * mm, v(1.5, 26.98) * mm], "startDerivative": vector(-22.5, 0) * mm, "endDerivative": vector(-22.5, 0) * mm});
            skFitSpline(sketch, "E314", {"points": [v(31.5, 26.23) * mm, v(24, 24.73) * mm, v(16.5, 23.23) * mm], "startDerivative": vector(-22.5, 0) * mm, "endDerivative": vector(-22.5, 0) * mm});
            skFitSpline(sketch, "E315", {"points": [v(16.5, 23.23) * mm, v(9, 24.73) * mm, v(1.5, 26.23) * mm], "startDerivative": vector(-22.5, 0) * mm, "endDerivative": vector(-22.5, 0) * mm});
            skFitSpline(sketch, "E316", {"points": [v(31.5, 24.73) * mm, v(24, 23.23) * mm, v(16.5, 21.73) * mm], "startDerivative": vector(-22.5, 0) * mm, "endDerivative": vector(-22.5, 0) * mm});
            skFitSpline(sketch, "E317", {"points": [v(16.5, 21.73) * mm, v(9, 23.23) * mm, v(1.5, 24.73) * mm], "startDerivative": vector(-22.5, 0) * mm, "endDerivative": vector(-22.5, 0) * mm});
            skFitSpline(sketch, "E318", {"points": [v(31.5, 23.98) * mm, v(24, 22.48) * mm, v(16.5, 20.98) * mm], "startDerivative": vector(-22.5, 0) * mm, "endDerivative": vector(-22.5, 0) * mm});
            skFitSpline(sketch, "E319", {"points": [v(16.5, 20.98) * mm, v(9, 22.48) * mm, v(1.5, 23.98) * mm], "startDerivative": vector(-22.5, 0) * mm, "endDerivative": vector(-22.5, 0) * mm});
            skPoint(sketch, "E320", {"position": v(15.75, 23.64) * mm});
            skPoint(sketch, "E321", {"position": v(17.25, 23.64) * mm});
            skLineSegment(sketch, "E322", {"start": v(17.25, 23.24) * mm, "end": v(17.25, 21.74) * mm});
            skLineSegment(sketch, "E323", {"start": v(15.75, 36.72) * mm, "end": v(15.75, 38.22) * mm});
            skLineSegment(sketch, "E324", {"start": v(17.25, 38.22) * mm, "end": v(17.25, 36.72) * mm});
            skLineSegment(sketch, "E325", {"start": v(17.25, 16.49) * mm, "end": v(17.25, 20.99) * mm});
            skPoint(sketch, "E326", {"position": v(15.75, 38.97) * mm});
            skPoint(sketch, "E327", {"position": v(17.25, 38.97) * mm});
            skLineSegment(sketch, "E328", {"start": v(15.75, 38.97) * mm, "end": v(15.75, 43.47) * mm});
            skLineSegment(sketch, "E329", {"start": v(17.25, 43.47) * mm, "end": v(17.25, 38.97) * mm});
            skPoint(sketch, "E330.start.orphan", {"position": v(1.5, 31.48) * mm});
            skLineSegment(sketch, "E331", {"start": v(-15.75, -7.49) * mm, "end": v(-35.75, -7.49) * mm});
            skLineSegment(sketch, "E332", {"start": v(-35.75, -7.49) * mm, "end": v(-35.75, -10.49) * mm});
            skLineSegment(sketch, "E333", {"start": v(-35.75, -10.49) * mm, "end": v(37.25, -10.49) * mm});
            skLineSegment(sketch, "E334", {"start": v(37.25, -10.49) * mm, "end": v(37.25, -7.49) * mm});
            skLineSegment(sketch, "E335", {"start": v(37.25, -7.49) * mm, "end": v(17.25, -7.49) * mm});
            skLineSegment(sketch, "E336.trimOffspring", {"start": v(15.75, -7.49) * mm, "end": v(-14.25, -7.49) * mm});
            skLineSegment(sketch, "E337", {"start": v(-15.75, 43.47) * mm, "end": v(-35.75, 43.47) * mm});
            skLineSegment(sketch, "E338", {"start": v(-35.75, 43.47) * mm, "end": v(-35.75, 46.47) * mm});
            skLineSegment(sketch, "E339", {"start": v(-35.75, 46.47) * mm, "end": v(37.25, 46.47) * mm});
            skLineSegment(sketch, "E340", {"start": v(37.25, 46.47) * mm, "end": v(37.25, 43.47) * mm});
            skLineSegment(sketch, "E341", {"start": v(37.25, 43.47) * mm, "end": v(17.25, 43.47) * mm});
            skLineSegment(sketch, "E342.trimOffspring", {"start": v(15.75, 43.47) * mm, "end": v(-14.25, 43.47) * mm});
            skLineSegment(sketch, "E343", {"start": v(33, 35.98) * mm, "end": v(36, 35.98) * mm});
            skLineSegment(sketch, "E344", {"start": v(36, 35.98) * mm, "end": v(36, 23.98) * mm});
            skLineSegment(sketch, "E345", {"start": v(36, 23.98) * mm, "end": v(33, 23.98) * mm});
            skLineSegment(sketch, "E346", {"start": v(33, 12) * mm, "end": v(36, 12) * mm});
            skLineSegment(sketch, "E347", {"start": v(36, 12) * mm, "end": v(36, 0) * mm});
            skLineSegment(sketch, "E348", {"start": v(36, 0) * mm, "end": v(33, 0) * mm});
            skLineSegment(sketch, "E349", {"start": v(-31.5, 0) * mm, "end": v(-34.5, 0) * mm});
            skLineSegment(sketch, "E350", {"start": v(-34.5, 0) * mm, "end": v(-34.5, 12) * mm});
            skLineSegment(sketch, "E351", {"start": v(-34.5, 12) * mm, "end": v(-31.5, 12) * mm});
            skLineSegment(sketch, "E352", {"start": v(-31.5, 23.98) * mm, "end": v(-34.5, 23.98) * mm});
            skLineSegment(sketch, "E353", {"start": v(-34.5, 23.98) * mm, "end": v(-34.5, 35.98) * mm});
            skLineSegment(sketch, "E354", {"start": v(-34.5, 35.98) * mm, "end": v(-31.5, 35.98) * mm});
            skSolve(sketch);
        }
        {
            var Q0;
            Q0 = qSketchRegion(id + "F0", true);
            extrude(context, id + "F1", {"entities" : qUnion([Q0]), "depth" : 25 * mm, "offsetDistance" : 25 * mm});
        }
    });
